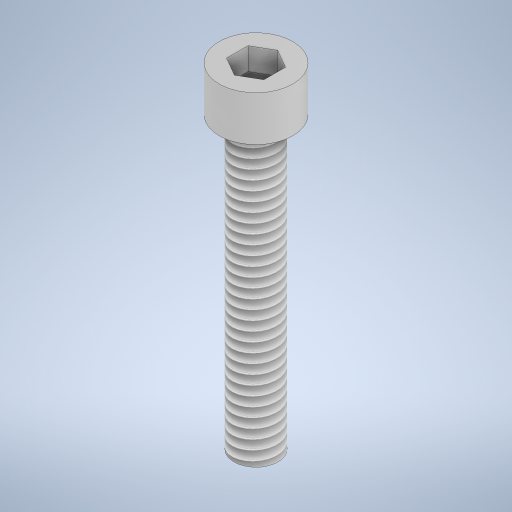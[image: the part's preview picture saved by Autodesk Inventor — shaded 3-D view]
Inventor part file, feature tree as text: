
AUTODESK INVENTOR PART (.ipt)
format: ipt  version: 2024 (Build 280153000, 153)  size: 289,280 bytes
history: native  units: in
note: dims shown in document units (in); Inventor stores cm internally (conversion verified against a paired STEP export)
features: extrude x3, sketch x3, thread x1
ambient origin geometry x8: Origin, YZ Plane, XZ Plane, XY Plane, X Axis, Y Axis, Z Axis, Center Point
bodies: Solid1 (feature_tree)
feature tree (7):
  extrude  "Extrusion1"  Depth=0.775in TaperAngle=0.0deg
  extrude  "Extrusion2"  Depth=0.12in TaperAngle=0.0deg
  extrude  "Extrusion3"  Depth=0.06in TaperAngle=0.0deg
  thread  "Thread1"  [1 undecoded]
  sketch  "Sketch1"  dims[d0=0.1181in d1=0.775in d2=0.0in]
  sketch  "Sketch2"  dims[d3=0.1969in d4=0.12in d5=0.0in]
  sketch  "Sketch3"  dims[d6=0.05in d7=0.06in d8=0.0in d9=0.775in d10=0.0in]
note: 1 required parameter value undecoded (feature->parameter linkage not recoverable at this tier; creation-order binding heuristic only, values carry confidence <= 0.55)
